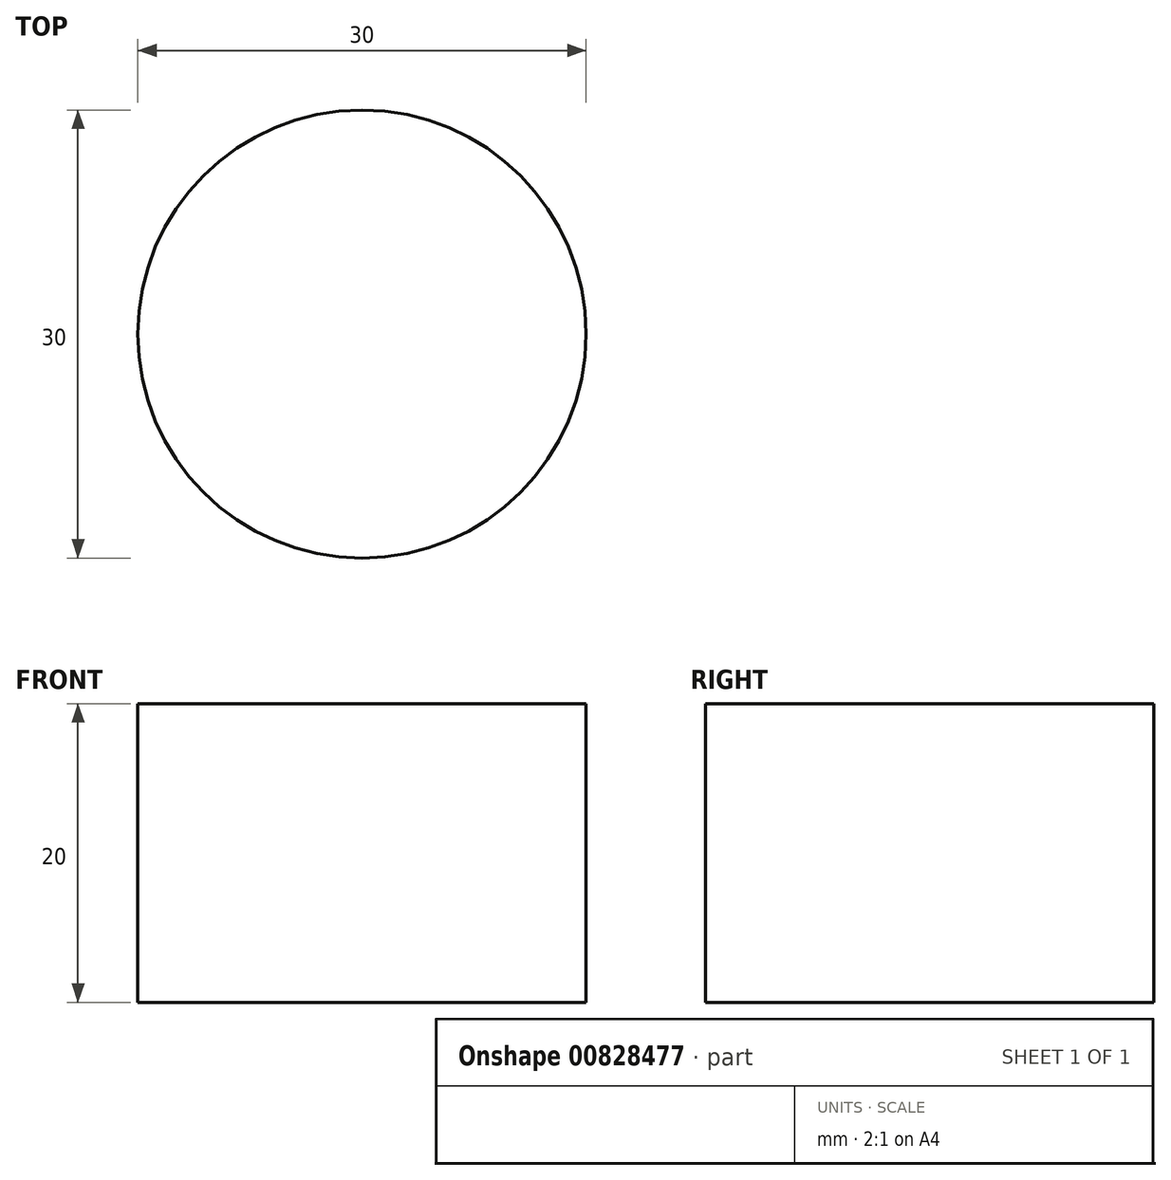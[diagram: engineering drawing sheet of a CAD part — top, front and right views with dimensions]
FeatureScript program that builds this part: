
annotation { "Feature Type Name" : "Feature", "Feature Type Description" : "" }
export const myFeature = defineFeature(function(context is Context, id is Id, definition is map)
    precondition{}
    {
        {
            var Q0;
            Q0=qCreatedBy(makeId("Top.planeOp"),FACE);
            var sketch = newSketch(context, id + "F0", { "sketchPlane" : qUnion([Q0])});
            skCircle(sketch, "E0", {"center": v(0, 0) * mm, "radius": 15 * mm});
            skSolve(sketch);
        }
        {
            var Q0;
            Q0 = qSketchRegion(id + "F0", true);
            extrude(context, id + "F1", {"entities" : qUnion([Q0]), "depth" : 20 * mm, "offsetDistance" : 25 * mm});
        }
    });
